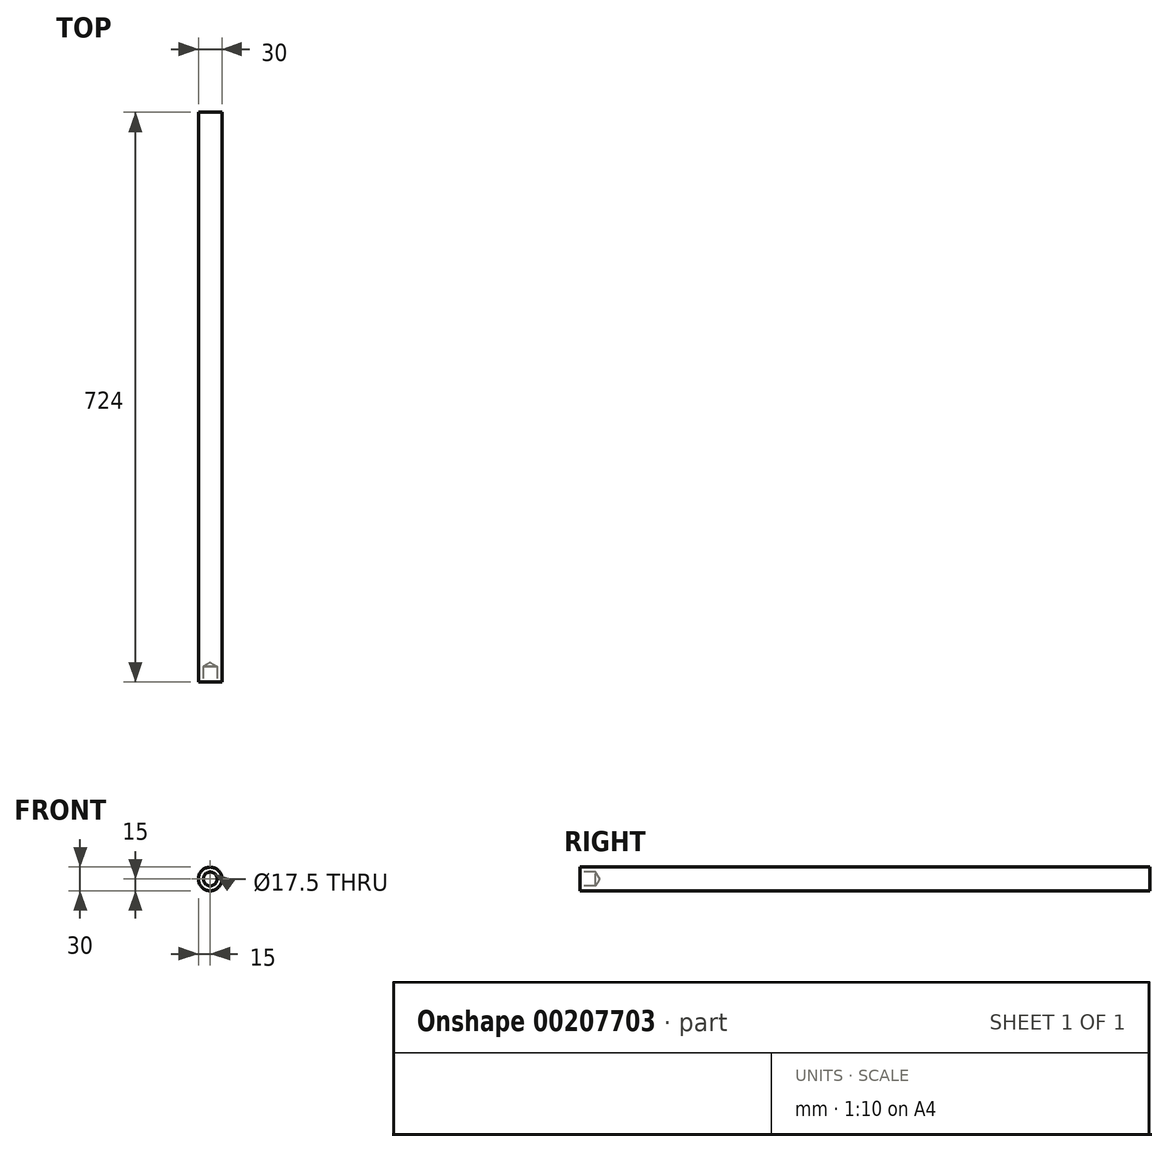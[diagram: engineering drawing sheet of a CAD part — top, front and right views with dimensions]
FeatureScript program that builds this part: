
annotation { "Feature Type Name" : "Feature", "Feature Type Description" : "" }
export const myFeature = defineFeature(function(context is Context, id is Id, definition is map)
    precondition{}
    {
        {
            var Q0;
            Q0=qCreatedBy(makeId("Front.planeOp"),FACE);
            var sketch = newSketch(context, id + "F0", { "sketchPlane" : qUnion([Q0])});
            skCircle(sketch, "E0", {"center": v(0, 0) * mm, "radius": 15 * mm});
            skSolve(sketch);
        }
        {
            var Q0;
            Q0 = qSketchRegion(id + "F0", true);
            extrude(context, id + "F1", {"entities" : qUnion([Q0]), "endBound" : BoundingType.SYMMETRIC, "depth" : 724 * mm});
        }
        {
            var Q0;
            Q0=makeQuery(id+"F1.opExtrude","CAP_FACE",FACE,{"disambiguationData":[OSD([sQuery(id+"F0.wireOp",EDGE,"E0")])],"isStart":false});
            var sketch = newSketch(context, id + "F2", { "sketchPlane" : qUnion([Q0])});
            skCircle(sketch, "E1", {"center": v(0, 0) * mm, "radius": 15 * mm});
            skSolve(sketch);
        }
        {
            var Q0;
            Q0=sQuery(id+"F2.wireOp",VERTEX,"E1.center");
            var Q1;
            Q1=makeQuery(id+"F1.opExtrude","SWEPT_BODY",BODY,{"disambiguationData":[OSD([sQuery(id+"F0.wireOp",EDGE,"E0")])]});
            hole(context, id + "F3", {"style" : HoleStyle.SIMPLE, "endStyle" : HoleEndStyle.BLIND, "standardTappedOrClearance" : lookupTablePath({ "standard" : "ISO", "engagement" : "75%", "pitch" : "2.5 mm", "size" : "M20", "type" : "Tapped" }), "standardBlindInLast" : lookupTablePath({ "standard" : "ISO", "engagement" : "75%", "pitch" : "2.5 mm", "size" : "M20", "type" : "Tapped" }), "holeDiameter" : 17.5 * mm, "showTappedDepth" : true, "holeDepth" : 20 * mm, "tappedDepth" : 12.5 * mm, "tapClearance" : 3, "locations" : qUnion([Q0]), "scope" : qUnion([Q1]), "majorDiameter" : 20 * mm});
        }
    });
